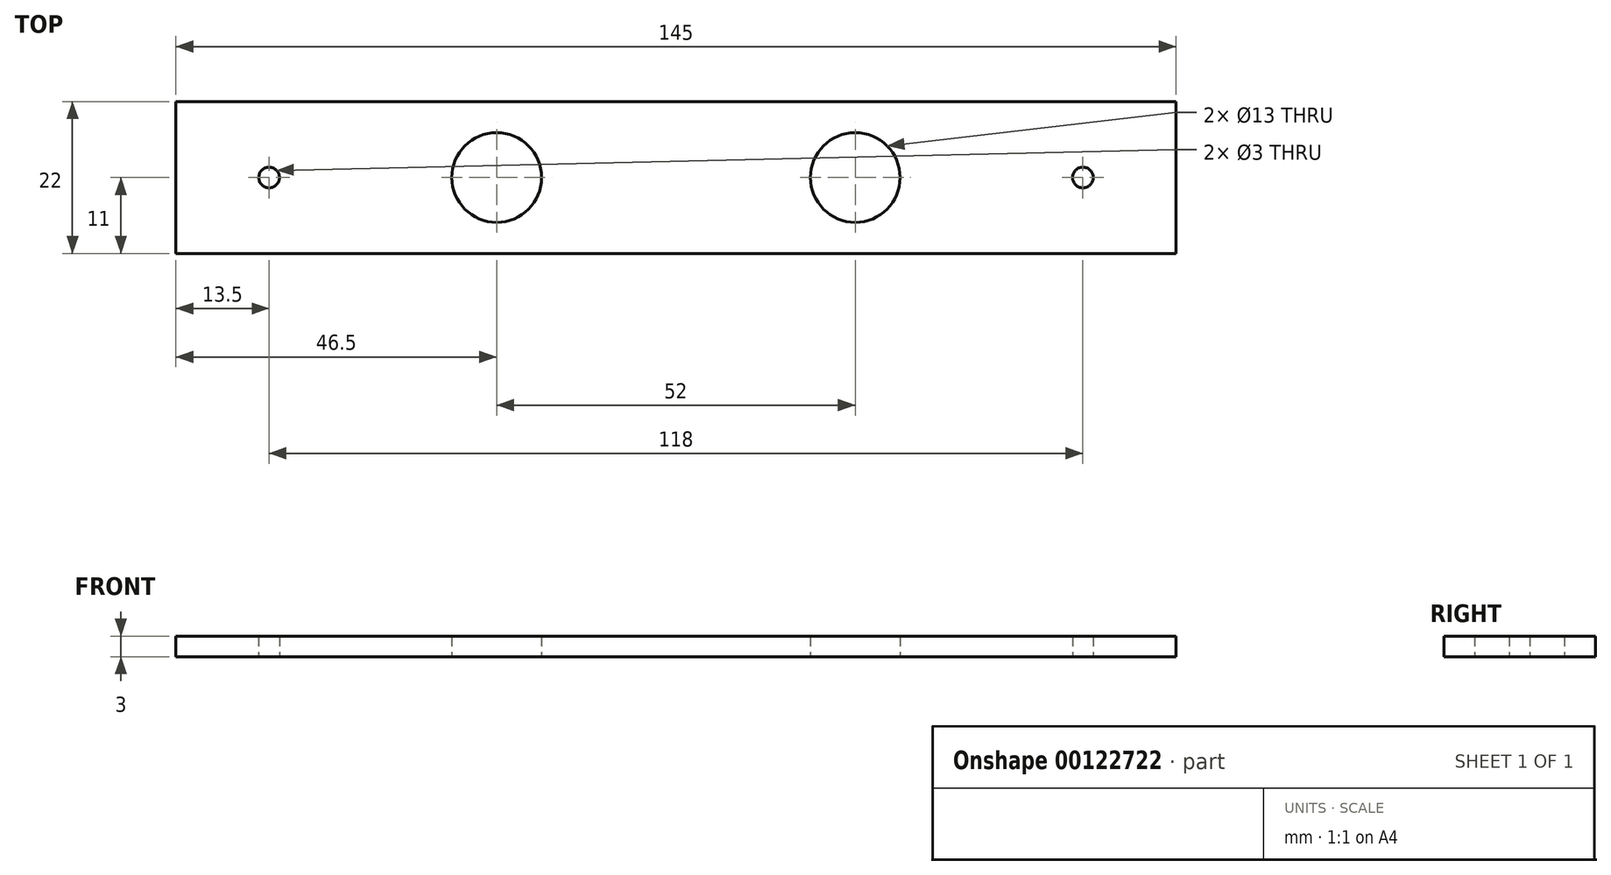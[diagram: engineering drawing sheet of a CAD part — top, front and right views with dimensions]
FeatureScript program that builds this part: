
annotation { "Feature Type Name" : "Feature", "Feature Type Description" : "" }
export const myFeature = defineFeature(function(context is Context, id is Id, definition is map)
    precondition{}
    {
        {
            var Q0;
            Q0=qCreatedBy(makeId("Top.planeOp"),FACE);
            var sketch = newSketch(context, id + "F0", { "sketchPlane" : qUnion([Q0])});
            skLineSegment(sketch, "E0.bottom", {"start": v(0, 0) * mm, "end": v(145, 0) * mm});
            skLineSegment(sketch, "E0.top", {"start": v(0, -22) * mm, "end": v(145, -22) * mm});
            skLineSegment(sketch, "E0.left", {"start": v(0, 0) * mm, "end": v(0, -22) * mm});
            skLineSegment(sketch, "E0.right", {"start": v(145, 0) * mm, "end": v(145, -22) * mm});
            skCircle(sketch, "E1", {"center": v(46.5, -11) * mm, "radius": 6.5 * mm});
            skCircle(sketch, "E2", {"center": v(98.5, -11) * mm, "radius": 6.5 * mm});
            skCircle(sketch, "E3", {"center": v(13.5, -11) * mm, "radius": 1.5 * mm});
            skCircle(sketch, "E4", {"center": v(131.5, -11) * mm, "radius": 1.5 * mm});
            skSolve(sketch);
        }
        {
            var Q0;
            Q0=qSketchRegion(id+"F0",true);
            extrude(context, id + "F1", {"entities" : qUnion([Q0]), "depth" : 3 * mm});
        }
    });
